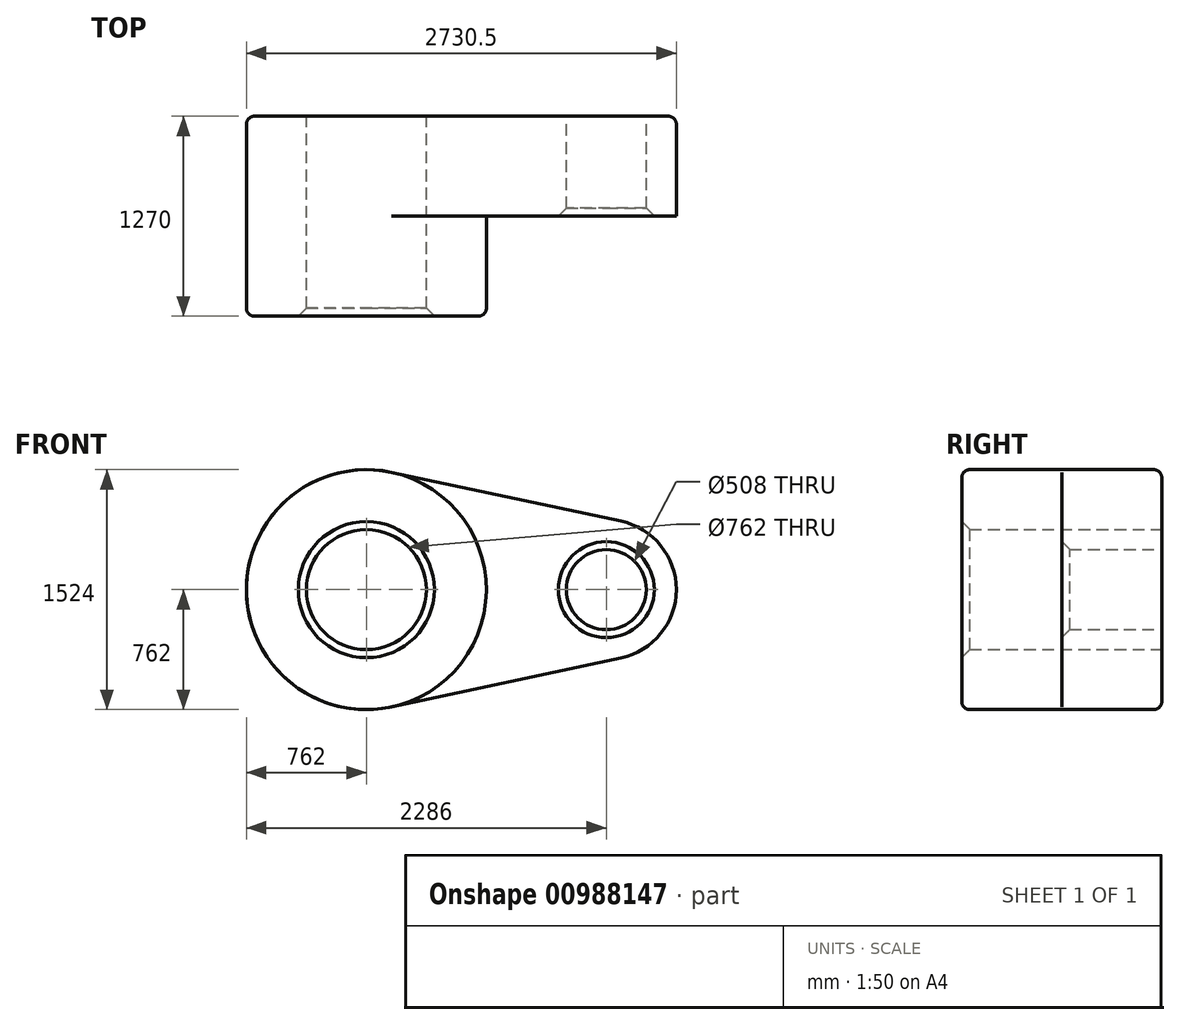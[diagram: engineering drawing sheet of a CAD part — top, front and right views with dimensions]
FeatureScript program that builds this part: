
annotation { "Feature Type Name" : "Feature", "Feature Type Description" : "" }
export const myFeature = defineFeature(function(context is Context, id is Id, definition is map)
    precondition{}
    {
        {
            var Q0;
            Q0=qCreatedBy(makeId("Front.planeOp"),FACE);
            var sketch = newSketch(context, id + "F0", { "sketchPlane" : qUnion([Q0])});
            skCircle(sketch, "E0", {"center": v(0, 0) * mm, "radius": 762 * mm});
            skCircle(sketch, "E1", {"center": v(1524, 0) * mm, "radius": 444.5 * mm});
            skLineSegment(sketch, "E2", {"start": v(158.75, 745.28) * mm, "end": v(1616.6, 434.75) * mm});
            skLineSegment(sketch, "E3", {"start": v(158.75, -745.28) * mm, "end": v(1616.6, -434.75) * mm});
            skCircle(sketch, "E4", {"center": v(0, 0) * mm, "radius": 381 * mm});
            skCircle(sketch, "E5", {"center": v(1524, 0) * mm, "radius": 254 * mm});
            skSolve(sketch);
        }
        {
            var Q0;
            {var subQ0=sQuery(id+"F0.wireOp",EDGE,"E2");Q0=makeQuery(id+"F0.imprint","IMPRINT",FACE,{"disambiguationData":[TD([[makeQuery(id+"F0.imprint","IMPRINT",EDGE,{"derivedFrom":subQ0}),-1.0]])]});}
            var Q1;
            Q1=makeQuery(id+"F0.imprint","IMPRINT",FACE,{"disambiguationData":[TD([[makeQuery(id+"F0.imprint","IMPRINT",EDGE,{"derivedFrom":sQuery(id+"F0.wireOp",EDGE,"E4")}),-1.0]])]});
            var Q2;
            Q2=makeQuery(id+"F0.imprint","IMPRINT",FACE,{"disambiguationData":[TD([[makeQuery(id+"F0.imprint","IMPRINT",EDGE,{"derivedFrom":sQuery(id+"F0.wireOp",EDGE,"E5")}),-1.0]])]});
            extrude(context, id + "F1", {"entities" : qUnion([Q0, Q1, Q2]), "depth" : 635 * mm, "offsetDistance" : 25.4 * mm});
        }
        {
            var Q0;
            Q0=makeQuery(id+"F0.imprint","IMPRINT",FACE,{"disambiguationData":[TD([[makeQuery(id+"F0.imprint","IMPRINT",EDGE,{"derivedFrom":sQuery(id+"F0.wireOp",EDGE,"E4")}),-1.0]])]});
            extrude(context, id + "F2", {"entities" : qUnion([Q0]), "operationType" : NewBodyOperationType.ADD, "depth" : 1270 * mm, "offsetDistance" : 25.4 * mm});
        }
        {
            var Q0;
            Q0=makeQuery(id+"F2.opExtrude","CAP_EDGE",EDGE,{"disambiguationData":[OSD([sQuery(id+"F0.wireOp",EDGE,"E0")])],"isStart":false});
            var Q1;
            Q1=makeQuery(id+"F1.opExtrude","CAP_EDGE",EDGE,{"disambiguationData":[OSD([sQuery(id+"F0.wireOp",EDGE,"E0")])],"isStart":true});
            var Q2;
            Q2=makeQuery(id+"F1.opExtrude","CAP_EDGE",EDGE,{"disambiguationData":[OSD([sQuery(id+"F0.wireOp",EDGE,"E2")])],"isStart":true});
            var Q3;
            Q3=makeQuery(id+"F1.opExtrude","CAP_EDGE",EDGE,{"disambiguationData":[OSD([sQuery(id+"F0.wireOp",EDGE,"E1")])],"isStart":true});
            var Q4;
            Q4=makeQuery(id+"F1.opExtrude","CAP_EDGE",EDGE,{"disambiguationData":[OSD([sQuery(id+"F0.wireOp",EDGE,"E3")])],"isStart":true});
            fillet(context, id + "F3", {"entities" : qUnion([Q0, Q1, Q2, Q3, Q4]), "radius" : 50.8 * mm, "tangentPropagation" : true, "allowEdgeOverflow" : false});
        }
        {
            var Q0;
            Q0=makeQuery(id+"F2.opExtrude","CAP_EDGE",EDGE,{"disambiguationData":[OSD([sQuery(id+"F0.wireOp",EDGE,"E4")])],"isStart":false});
            var Q1;
            Q1=makeQuery(id+"F1.opExtrude","CAP_EDGE",EDGE,{"disambiguationData":[OSD([sQuery(id+"F0.wireOp",EDGE,"E5")])],"isStart":false});
            chamfer(context, id + "F4", {"entities" : qUnion([Q0, Q1]), "width" : 50.8 * mm, "tangentPropagation" : true});
        }
    });
